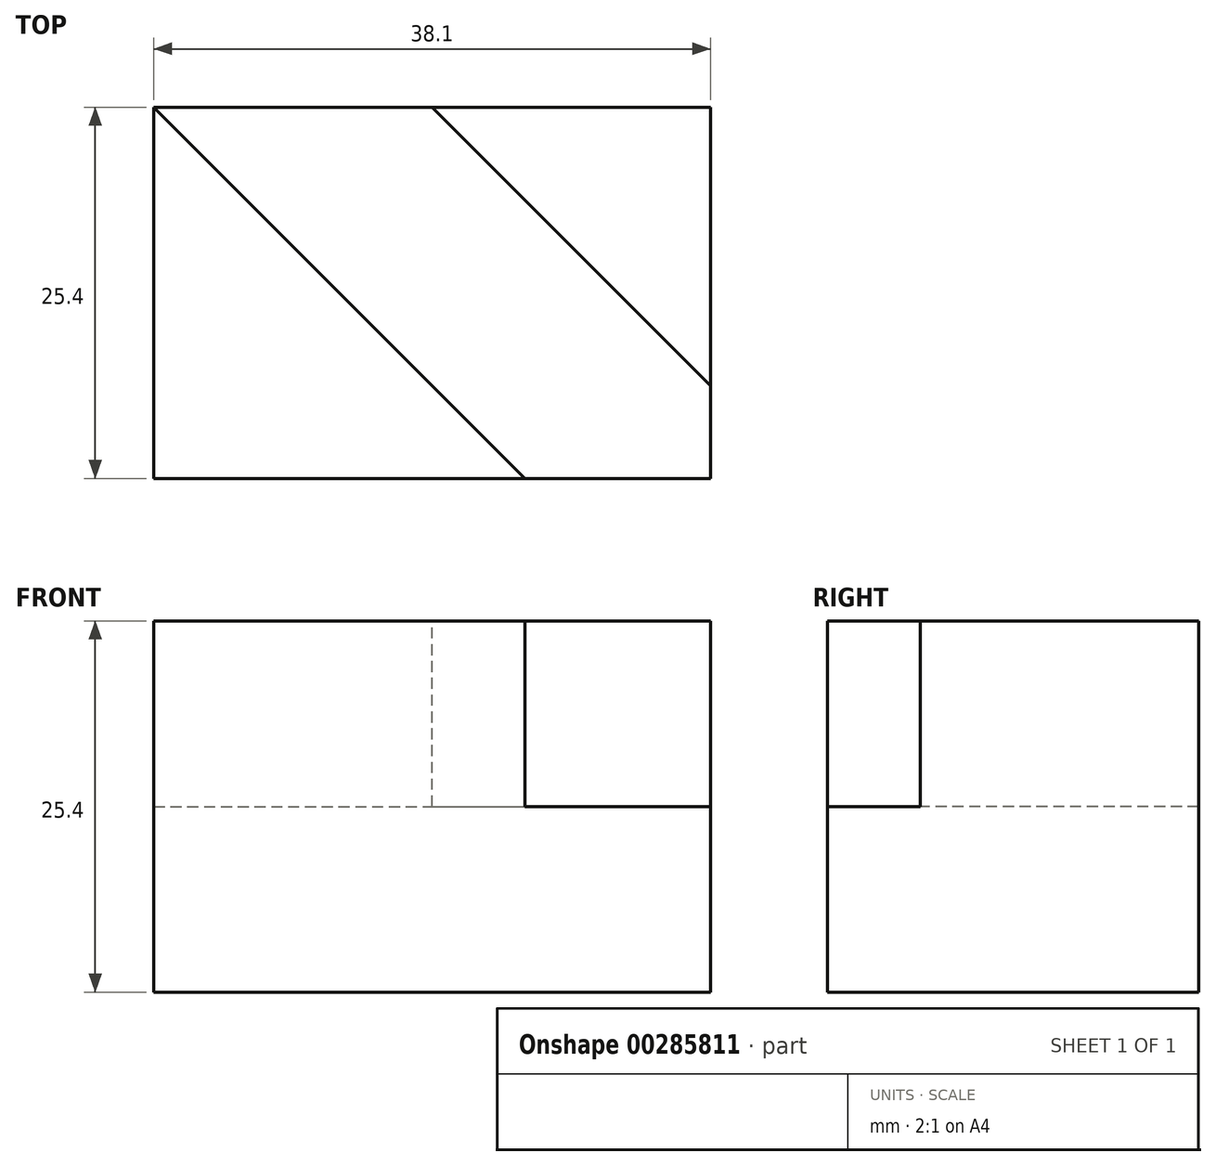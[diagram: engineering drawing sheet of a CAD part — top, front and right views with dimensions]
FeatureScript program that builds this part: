
annotation { "Feature Type Name" : "Feature", "Feature Type Description" : "" }
export const myFeature = defineFeature(function(context is Context, id is Id, definition is map)
    precondition{}
    {
        {
            var Q0;
            Q0=qCreatedBy(makeId("Front.planeOp"),FACE);
            var sketch = newSketch(context, id + "F0", { "sketchPlane" : qUnion([Q0])});
            skLineSegment(sketch, "E0.bottom", {"start": v(0, 0) * mm, "end": v(38.1, 0) * mm});
            skLineSegment(sketch, "E0.top", {"start": v(0, 25.4) * mm, "end": v(38.1, 25.4) * mm});
            skLineSegment(sketch, "E0.left", {"start": v(0, 0) * mm, "end": v(0, 25.4) * mm});
            skLineSegment(sketch, "E0.right", {"start": v(38.1, 0) * mm, "end": v(38.1, 25.4) * mm});
            skSolve(sketch);
        }
        {
            var Q0;
            Q0=makeQuery(id+"F0.imprint","IMPRINT",FACE,{"disambiguationData":[TD([[makeQuery(id+"F0.imprint","IMPRINT",EDGE,{"derivedFrom":sQuery(id+"F0.wireOp",EDGE,"E0.bottom")}),1.0]])]});
            extrude(context, id + "F1", {"entities" : qUnion([Q0]), "depth" : 25.4 * mm, "symmetric" : true});
        }
        {
            var Q0;
            Q0=makeQuery(id+"F1.opExtrude","SWEPT_FACE",FACE,{"disambiguationData":[OSD([sQuery(id+"F0.wireOp",EDGE,"E0.top")])]});
            var sketch = newSketch(context, id + "F2", { "sketchPlane" : qUnion([Q0])});
            skLineSegment(sketch, "E1", {"start": v(0, 12.7) * mm, "end": v(25.4, -12.7) * mm});
            skLineSegment(sketch, "E2", {"start": v(19.05, 12.7) * mm, "end": v(38.1, -6.35) * mm});
            skSolve(sketch);
        }
        {
            var Q0;
            {var subQ5=sQuery(id+"F2.wireOp",EDGE,"E1");Q0=makeQuery(id+"F2.imprint","IMPRINT",FACE,{"disambiguationData":[TD([[makeQuery(id+"F2.imprint","IMPRINT",EDGE,{"derivedFrom":subQ5}),1.0]])]});}
            extrude(context, id + "F3", {"entities" : qUnion([Q0]), "operationType" : NewBodyOperationType.REMOVE, "oppositeDirection" : true, "depth" : 12.7 * mm});
        }
    });
